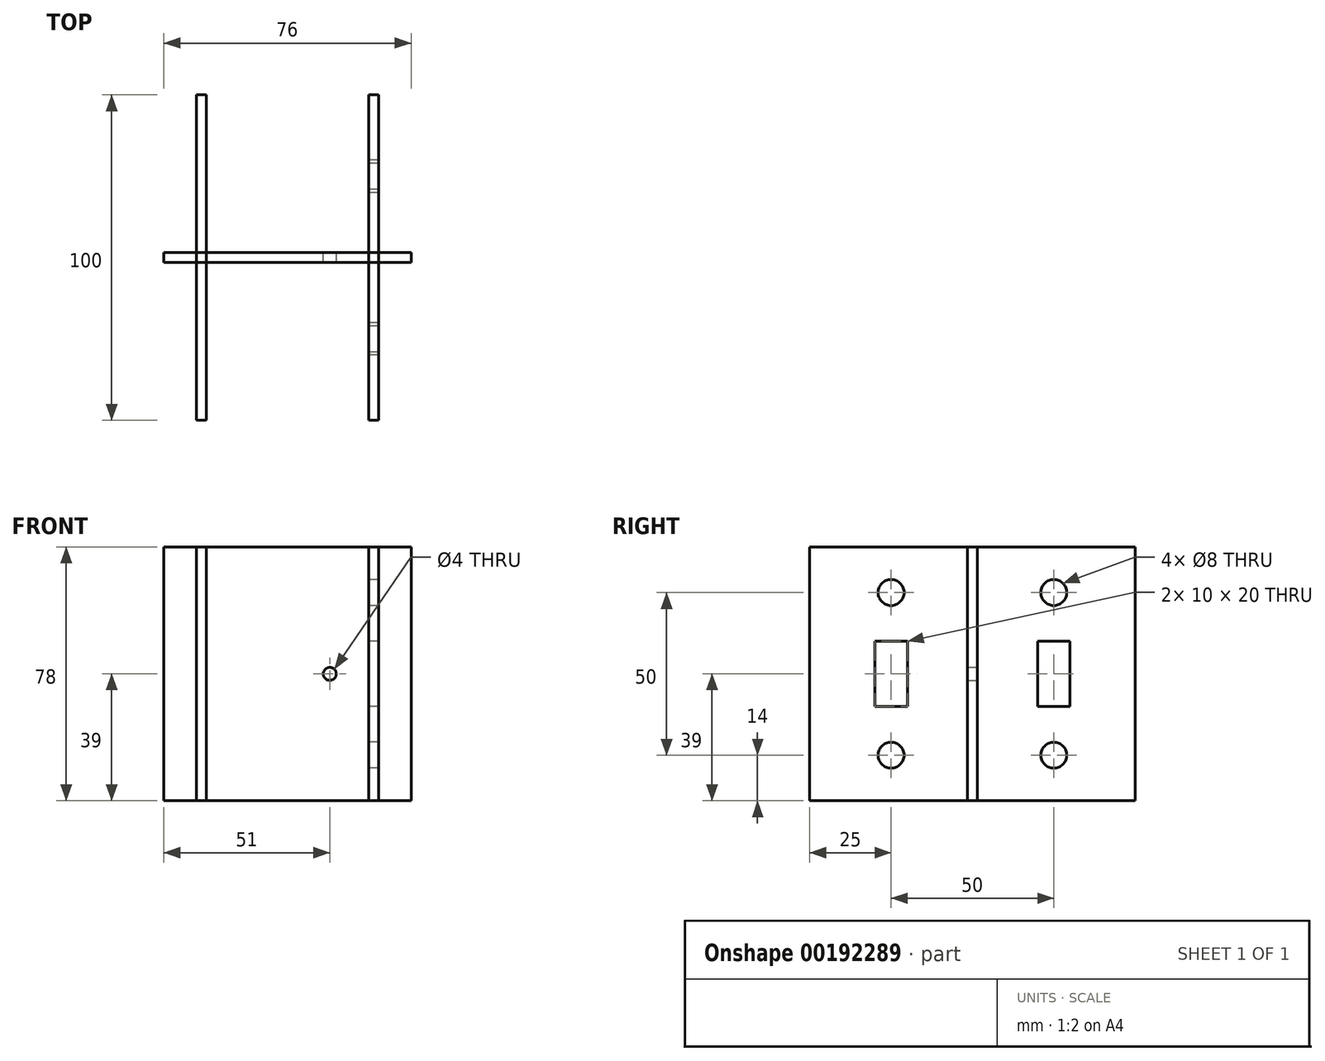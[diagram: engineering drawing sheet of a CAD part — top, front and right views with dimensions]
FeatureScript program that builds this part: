
annotation { "Feature Type Name" : "Feature", "Feature Type Description" : "" }
export const myFeature = defineFeature(function(context is Context, id is Id, definition is map)
    precondition{}
    {
        {
            var Q0;
            Q0=qCreatedBy(makeId("Right.planeOp"),FACE);
            var sketch = newSketch(context, id + "F0", { "sketchPlane" : qUnion([Q0])});
            skLineSegment(sketch, "E0.bottom", {"start": v(-50, 39) * mm, "end": v(50, 39) * mm});
            skLineSegment(sketch, "E0.top", {"start": v(-50, -39) * mm, "end": v(50, -39) * mm});
            skLineSegment(sketch, "E0.left", {"start": v(-50, 39) * mm, "end": v(-50, -39) * mm});
            skLineSegment(sketch, "E0.right", {"start": v(50, 39) * mm, "end": v(50, -39) * mm});
            skPoint(sketch, "E0.middle", {"position": v(0, 0) * mm});
            skLineSegment(sketch, "E1.bottom", {"start": v(-30, 10) * mm, "end": v(-20, 10) * mm});
            skLineSegment(sketch, "E1.top", {"start": v(-30, -10) * mm, "end": v(-20, -10) * mm});
            skLineSegment(sketch, "E1.left", {"start": v(-30, 10) * mm, "end": v(-30, -10) * mm});
            skLineSegment(sketch, "E1.right", {"start": v(-20, 10) * mm, "end": v(-20, -10) * mm});
            skPoint(sketch, "E1.middle", {"position": v(-25, 0) * mm});
            skLineSegment(sketch, "E2.bottom", {"start": v(20, 10) * mm, "end": v(30, 10) * mm});
            skLineSegment(sketch, "E2.top", {"start": v(20, -10) * mm, "end": v(30, -10) * mm});
            skLineSegment(sketch, "E2.left", {"start": v(20, 10) * mm, "end": v(20, -10) * mm});
            skLineSegment(sketch, "E2.right", {"start": v(30, 10) * mm, "end": v(30, -10) * mm});
            skPoint(sketch, "E2.middle", {"position": v(25, 0) * mm});
            skCircle(sketch, "E3", {"center": v(-25, 25) * mm, "radius": 4 * mm});
            skCircle(sketch, "E4", {"center": v(25, 25) * mm, "radius": 4 * mm});
            skCircle(sketch, "E5", {"center": v(-25, -25) * mm, "radius": 4 * mm});
            skCircle(sketch, "E6", {"center": v(25, -25) * mm, "radius": 4 * mm});
            skPoint(sketch, "E6.centerSnap0", {"position": v(25, -10) * mm});
            skLineSegment(sketch, "E7", {"start": v(-25, 25) * mm, "end": v(-25, -25) * mm, "construction": true});
            skSolve(sketch);
        }
        {
            var Q0;
            Q0=makeQuery(id+"F0.imprint","IMPRINT",FACE,{"disambiguationData":[TD([[makeQuery(id+"F0.imprint","IMPRINT",EDGE,{"derivedFrom":sQuery(id+"F0.wireOp",EDGE,"E0.bottom")}),-1.0]])]});
            extrude(context, id + "F1", {"entities" : qUnion([Q0]), "depth" : 3 * mm});
        }
        {
            var Q0;
            Q0=makeQuery(id+"F1.opExtrude","CAP_FACE",FACE,{"disambiguationData":[OSD([sQuery(id+"F0.wireOp",EDGE,"E0.bottom"),sQuery(id+"F0.wireOp",EDGE,"E0.top"),sQuery(id+"F0.wireOp",EDGE,"E0.left"),sQuery(id+"F0.wireOp",EDGE,"E0.right"),sQuery(id+"F0.wireOp",EDGE,"E1.bottom"),sQuery(id+"F0.wireOp",EDGE,"E1.top"),sQuery(id+"F0.wireOp",EDGE,"E1.left"),sQuery(id+"F0.wireOp",EDGE,"E1.right"),sQuery(id+"F0.wireOp",EDGE,"E2.bottom"),sQuery(id+"F0.wireOp",EDGE,"E2.top"),sQuery(id+"F0.wireOp",EDGE,"E2.left"),sQuery(id+"F0.wireOp",EDGE,"E2.right"),sQuery(id+"F0.wireOp",EDGE,"E3"),sQuery(id+"F0.wireOp",EDGE,"E4"),sQuery(id+"F0.wireOp",EDGE,"E5"),sQuery(id+"F0.wireOp",EDGE,"E6")])],"isStart":true});
            cPlane(context, id + "F2", {"entities" : qUnion([Q0]), "cplaneType" : CPlaneType.OFFSET, "offset" : 50 * mm, "width" : 150 * mm, "height" : 150 * mm});
        }
        {
            var Q0;
            Q0=qCreatedBy(id+"F2.planeOp",FACE);
            var sketch = newSketch(context, id + "F3", { "sketchPlane" : qUnion([Q0])});
            skLineSegment(sketch, "E8.0", {"start": v(-50, 39) * mm, "end": v(-50, -39) * mm});
            skLineSegment(sketch, "E8.1", {"start": v(50, 39) * mm, "end": v(-50, 39) * mm});
            skLineSegment(sketch, "E8.2", {"start": v(50, 39) * mm, "end": v(50, -39) * mm});
            skLineSegment(sketch, "E8.3", {"start": v(50, -39) * mm, "end": v(-50, -39) * mm});
            skSolve(sketch);
        }
        {
            var Q0;
            Q0=makeQuery(id+"F3.imprint","IMPRINT",FACE,{"disambiguationData":[TD([[makeQuery(id+"F3.imprint","IMPRINT",EDGE,{"derivedFrom":sQuery(id+"F3.wireOp",EDGE,"E8.0")}),1.0]])]});
            extrude(context, id + "F4", {"entities" : qUnion([Q0]), "depth" : 3 * mm});
        }
        {
            var Q0;
            Q0=qCreatedBy(makeId("Front.planeOp"),FACE);
            var sketch = newSketch(context, id + "F5", { "sketchPlane" : qUnion([Q0])});
            skLineSegment(sketch, "E9.0", {"start": v(-53, 39) * mm, "end": v(-53, -39) * mm});
            skLineSegment(sketch, "E10.0", {"start": v(3, 39) * mm, "end": v(3, -39) * mm});
            skLineSegment(sketch, "E11.bottom", {"start": v(-63, 39) * mm, "end": v(13, 39) * mm});
            skLineSegment(sketch, "E11.top", {"start": v(-63, -39) * mm, "end": v(13, -39) * mm});
            skLineSegment(sketch, "E11.left", {"start": v(-63, 39) * mm, "end": v(-63, -39) * mm});
            skLineSegment(sketch, "E11.right", {"start": v(13, 39) * mm, "end": v(13, -39) * mm});
            skPoint(sketch, "E11.middle", {"position": v(-25, 0) * mm});
            skLineSegment(sketch, "E12", {"start": v(-53, 0) * mm, "end": v(3, 0) * mm, "construction": true});
            skCircle(sketch, "E13", {"center": v(-12, 0) * mm, "radius": 2 * mm});
            skSolve(sketch);
        }
        {
            var Q0;
            Q0 = qSketchRegion(id + "F5", true);
            extrude(context, id + "F6", {"entities" : qUnion([Q0]), "endBound" : BoundingType.SYMMETRIC, "depth" : 3 * mm});
        }
    });
